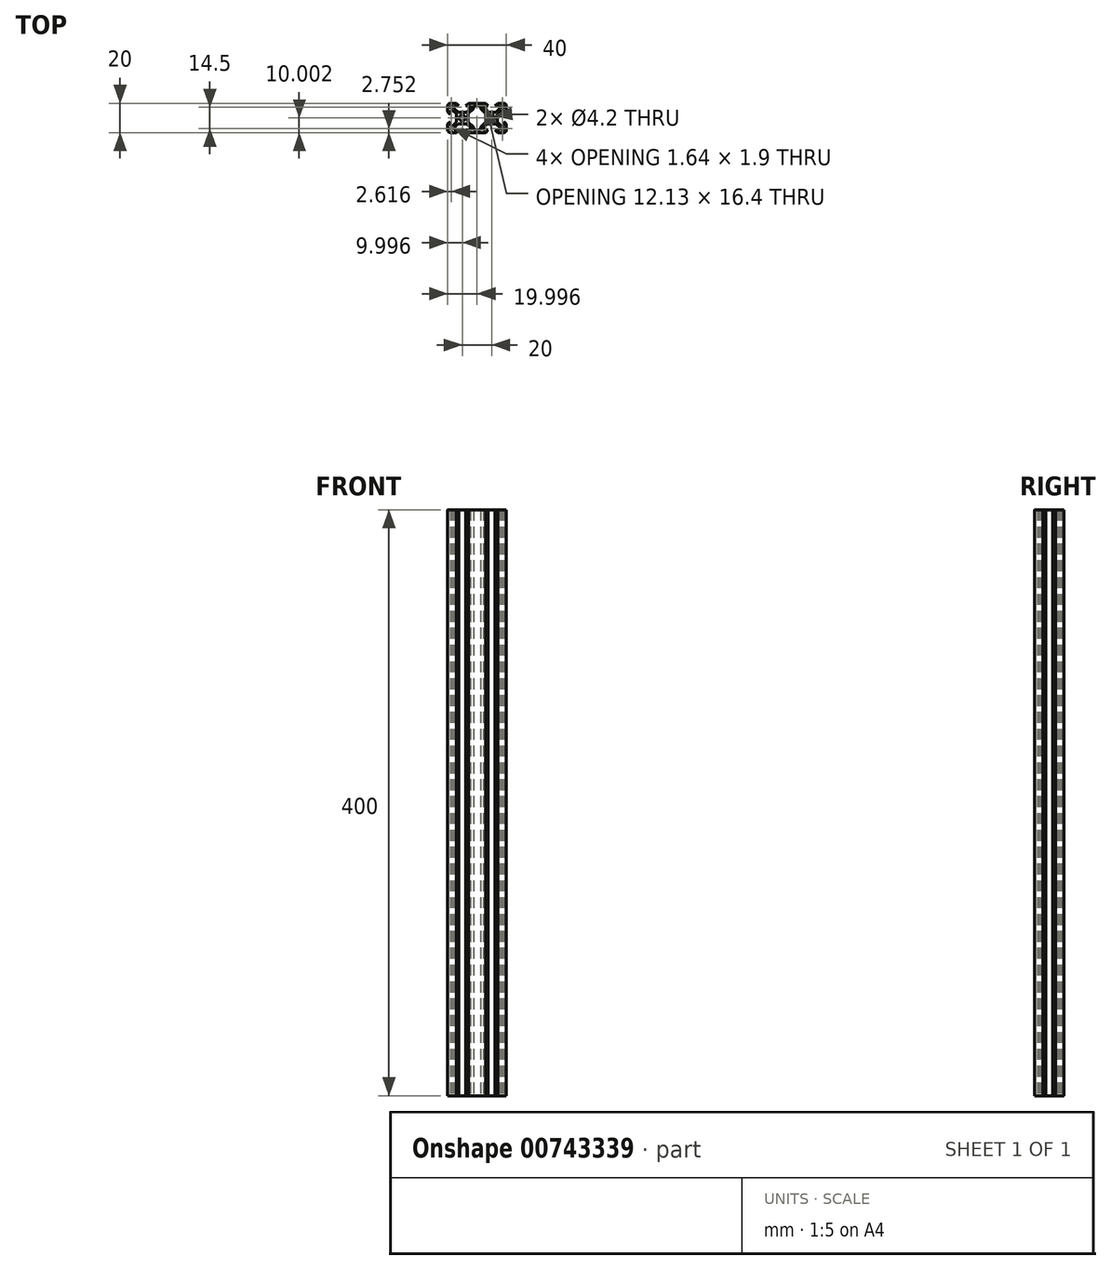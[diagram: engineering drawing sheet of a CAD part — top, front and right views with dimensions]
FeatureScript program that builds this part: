
annotation { "Feature Type Name" : "Feature", "Feature Type Description" : "" }
export const myFeature = defineFeature(function(context is Context, id is Id, definition is map)
    precondition{}
    {
        {
            var Q0;
            Q0=qCreatedBy(makeId("Top.planeOp"),FACE);
            var sketch = newSketch(context, id + "F0", { "sketchPlane" : qUnion([Q0])});
            skLineSegment(sketch, "E0.bottom", {"start": v(-44.81, 11.81) * mm, "end": v(-24.81, 11.81) * mm, "construction": true});
            skLineSegment(sketch, "E0.top", {"start": v(-44.81, -8.19) * mm, "end": v(-24.81, -8.19) * mm, "construction": true});
            skLineSegment(sketch, "E0.left", {"start": v(-44.81, 11.81) * mm, "end": v(-44.81, -8.19) * mm, "construction": true});
            skLineSegment(sketch, "E1", {"start": v(-44.81, 1.81) * mm, "end": v(-30.88, 1.81) * mm, "construction": true});
            skLineSegment(sketch, "E2", {"start": v(-34.81, 11.81) * mm, "end": v(-34.81, -8.19) * mm, "construction": true});
            skArc(sketch, "E3", {"start": v(-34.81, 3.91) * mm, "mid": v(-36.3, 3.3) * mm, "end": v(-36.91, 1.81) * mm});
            skLineSegment(sketch, "E4.left", {"start": v(-44.81, 10.01) * mm, "end": v(-44.81, 6) * mm});
            skLineSegment(sketch, "E4.right", {"start": v(-43.01, 10.01) * mm, "end": v(-43.01, 8.11) * mm});
            skLineSegment(sketch, "E5", {"start": v(-44.81, 11.81) * mm, "end": v(-34.81, 1.81) * mm, "construction": true});
            skLineSegment(sketch, "E6.MirrorCS", {"start": v(-43.01, 10.01) * mm, "end": v(-41.37, 10.01) * mm});
            skLineSegment(sketch, "E7.MirrorCS", {"start": v(-43.01, 11.81) * mm, "end": v(-39, 11.81) * mm});
            skLineSegment(sketch, "E8", {"start": v(-37.2, 10.01) * mm, "end": v(-39, 11.81) * mm});
            skLineSegment(sketch, "E9.MirrorCS", {"start": v(-43.01, 4.2) * mm, "end": v(-44.81, 6) * mm});
            skPoint(sketch, "E10.orphan", {"position": v(-37.2, 11.81) * mm});
            skPoint(sketch, "E11.orphan", {"position": v(-44.81, 4.2) * mm});
            skLineSegment(sketch, "E12.0", {"start": v(-41.3, 7.04) * mm, "end": v(-38.75, 4.65) * mm});
            skLineSegment(sketch, "E13.MirrorCS", {"start": v(-40.3, 8.11) * mm, "end": v(-37.65, 5.74) * mm});
            skPoint(sketch, "E14.orphan", {"position": v(-43.57, 9.18) * mm});
            skPoint(sketch, "E15.orphan", {"position": v(-42.6, 10.16) * mm});
            skLineSegment(sketch, "E16.top", {"start": v(-43.01, 8.11) * mm, "end": v(-42.43, 8.11) * mm});
            skLineSegment(sketch, "E17.MirrorCS", {"start": v(-41.37, 10.01) * mm, "end": v(-41.37, 9.07) * mm});
            skLineSegment(sketch, "E18", {"start": v(-40.3, 8.11) * mm, "end": v(-40.3, 10.01) * mm});
            skLineSegment(sketch, "E19.MirrorCS", {"start": v(-41.3, 7.04) * mm, "end": v(-43.01, 7.04) * mm});
            skLineSegment(sketch, "E20", {"start": v(-42.43, 8.11) * mm, "end": v(-41.37, 9.07) * mm});
            skLineSegment(sketch, "E21.trimOffspring", {"start": v(-43.01, 7.04) * mm, "end": v(-43.01, 4.2) * mm});
            skLineSegment(sketch, "E22.trimOffspring", {"start": v(-40.3, 10.01) * mm, "end": v(-37.2, 10.01) * mm});
            skPoint(sketch, "E16.right.end.orphan", {"position": v(-37.2, 8.37) * mm});
            skPoint(sketch, "E23.MirrorCS.end.orphan", {"position": v(-41.37, 4.2) * mm});
            skPoint(sketch, "E23.MirrorCS.start.orphan", {"position": v(-43.01, 4.2) * mm});
            skLineSegment(sketch, "E24", {"start": v(-38.75, 1.81) * mm, "end": v(-38.75, 4.65) * mm});
            skLineSegment(sketch, "E25.bottom", {"start": v(-37.65, 5.74) * mm, "end": v(-34.81, 5.74) * mm});
            skLineSegment(sketch, "E25.left", {"start": v(-38.75, 4.65) * mm, "end": v(-38.75, 1.81) * mm});
            skPoint(sketch, "E26.orphan", {"position": v(-38.75, 5.74) * mm});
            skPoint(sketch, "E27.orphan", {"position": v(-38.75, -2.12) * mm});
            skPoint(sketch, "E25.right.start.orphan", {"position": v(-30.88, 5.74) * mm});
            skArc(sketch, "E28", {"start": v(-43.01, 11.81) * mm, "mid": v(-44.29, 11.28) * mm, "end": v(-44.81, 10.01) * mm});
            skPoint(sketch, "E29.MirrorCS.start.orphan", {"position": v(-44.81, 11.81) * mm});
            skLineSegment(sketch, "E30.MirrorCS", {"start": v(-26.61, 11.81) * mm, "end": v(-30.62, 11.81) * mm});
            skLineSegment(sketch, "E31.MirrorCS", {"start": v(-32.42, 10.01) * mm, "end": v(-30.62, 11.81) * mm});
            skLineSegment(sketch, "E32.MirrorCS", {"start": v(-29.32, 10.01) * mm, "end": v(-32.42, 10.01) * mm});
            skLineSegment(sketch, "E33.MirrorCS", {"start": v(-29.32, 8.11) * mm, "end": v(-29.32, 10.01) * mm});
            skLineSegment(sketch, "E34.MirrorCS", {"start": v(-29.32, 8.11) * mm, "end": v(-31.98, 5.74) * mm});
            skLineSegment(sketch, "E35.MirrorCS", {"start": v(-31.98, 5.74) * mm, "end": v(-34.81, 5.74) * mm});
            skArc(sketch, "E36.MirrorCS", {"start": v(-34.81, 3.91) * mm, "mid": v(-33.33, 3.3) * mm, "end": v(-32.71, 1.81) * mm});
            skLineSegment(sketch, "E37.MirrorCS", {"start": v(-30.88, 4.65) * mm, "end": v(-30.88, 1.81) * mm});
            skArc(sketch, "E38.MirrorCS", {"start": v(-43.01, -8.19) * mm, "mid": v(-44.29, -7.66) * mm, "end": v(-44.81, -6.39) * mm});
            skLineSegment(sketch, "E39.MirrorCS", {"start": v(-44.81, -6.39) * mm, "end": v(-44.81, -2.38) * mm});
            skLineSegment(sketch, "E40.MirrorCS", {"start": v(-43.01, -0.58) * mm, "end": v(-44.81, -2.38) * mm});
            skLineSegment(sketch, "E41.MirrorCS", {"start": v(-43.01, -3.42) * mm, "end": v(-43.01, -0.58) * mm});
            skLineSegment(sketch, "E42.MirrorCS", {"start": v(-41.3, -3.42) * mm, "end": v(-43.01, -3.42) * mm});
            skLineSegment(sketch, "E43.MirrorCS", {"start": v(-41.3, -3.42) * mm, "end": v(-38.75, -1.03) * mm});
            skLineSegment(sketch, "E44.MirrorCS", {"start": v(-38.75, 1.81) * mm, "end": v(-38.75, -1.03) * mm});
            skLineSegment(sketch, "E45.MirrorCS", {"start": v(-42.43, -4.49) * mm, "end": v(-41.37, -5.44) * mm});
            skLineSegment(sketch, "E46.MirrorCS", {"start": v(-43.01, -4.49) * mm, "end": v(-42.43, -4.49) * mm});
            skLineSegment(sketch, "E47.MirrorCS", {"start": v(-43.01, -6.39) * mm, "end": v(-43.01, -4.49) * mm});
            skLineSegment(sketch, "E48.MirrorCS", {"start": v(-43.01, -6.39) * mm, "end": v(-41.37, -6.39) * mm});
            skLineSegment(sketch, "E49.MirrorCS", {"start": v(-43.01, -8.19) * mm, "end": v(-39, -8.19) * mm});
            skLineSegment(sketch, "E50.MirrorCS", {"start": v(-37.2, -6.39) * mm, "end": v(-39, -8.19) * mm});
            skLineSegment(sketch, "E51.MirrorCS", {"start": v(-40.3, -6.39) * mm, "end": v(-37.2, -6.39) * mm});
            skLineSegment(sketch, "E52.MirrorCS", {"start": v(-40.3, -4.49) * mm, "end": v(-40.3, -6.39) * mm});
            skLineSegment(sketch, "E53.MirrorCS", {"start": v(-40.3, -4.49) * mm, "end": v(-37.65, -2.12) * mm});
            skLineSegment(sketch, "E54.MirrorCS", {"start": v(-37.65, -2.12) * mm, "end": v(-34.81, -2.12) * mm});
            skArc(sketch, "E55.MirrorCS", {"start": v(-34.81, -0.29) * mm, "mid": v(-36.3, 0.33) * mm, "end": v(-36.91, 1.81) * mm});
            skLineSegment(sketch, "E56.MirrorCS", {"start": v(-41.37, -6.39) * mm, "end": v(-41.37, -5.44) * mm});
            skLineSegment(sketch, "E57.MirrorCS", {"start": v(-8.25, -6.39) * mm, "end": v(-8.25, -5.44) * mm});
            skLineSegment(sketch, "E58.MirrorCS", {"start": v(-8.25, 10.01) * mm, "end": v(-8.25, 9.07) * mm});
            skLineSegment(sketch, "E59.MirrorCS", {"start": v(-6.61, 8.11) * mm, "end": v(-7.2, 8.11) * mm});
            skLineSegment(sketch, "E60.MirrorCS", {"start": v(-6.61, -4.49) * mm, "end": v(-7.2, -4.49) * mm});
            skLineSegment(sketch, "E61.MirrorCS", {"start": v(-6.61, -8.19) * mm, "end": v(-10.62, -8.19) * mm});
            skLineSegment(sketch, "E62.MirrorCS", {"start": v(-23.01, 11.81) * mm, "end": v(-19, 11.81) * mm});
            skLineSegment(sketch, "E63.MirrorCS", {"start": v(-4.81, 10.01) * mm, "end": v(-4.81, 6) * mm});
            skLineSegment(sketch, "E64.MirrorCS", {"start": v(-6.61, 11.81) * mm, "end": v(-10.62, 11.81) * mm});
            skLineSegment(sketch, "E65.MirrorCS", {"start": v(-4.81, -6.39) * mm, "end": v(-4.81, -2.38) * mm});
            skLineSegment(sketch, "E66.MirrorCS", {"start": v(-6.61, 10.01) * mm, "end": v(-6.61, 8.11) * mm});
            skLineSegment(sketch, "E67.MirrorCS", {"start": v(-10.88, 1.81) * mm, "end": v(-10.88, 4.65) * mm});
            skPoint(sketch, "E68.MirrorP", {"position": v(-8.25, 4.2) * mm});
            skLineSegment(sketch, "E69.MirrorCS", {"start": v(-9.32, 10.01) * mm, "end": v(-12.42, 10.01) * mm});
            skLineSegment(sketch, "E70.MirrorCS", {"start": v(-6.61, 10.01) * mm, "end": v(-8.25, 10.01) * mm});
            skPoint(sketch, "E71.MirrorP", {"position": v(-6.05, 9.18) * mm});
            skLineSegment(sketch, "E72.MirrorCS", {"start": v(-9.32, -6.39) * mm, "end": v(-12.42, -6.39) * mm});
            skLineSegment(sketch, "E73.MirrorCS", {"start": v(-8.33, 7.04) * mm, "end": v(-10.88, 4.65) * mm});
            skLineSegment(sketch, "E74.MirrorCS", {"start": v(-8.33, 7.04) * mm, "end": v(-6.61, 7.04) * mm});
            skLineSegment(sketch, "E75.MirrorCS", {"start": v(-20.3, 10.01) * mm, "end": v(-17.2, 10.01) * mm});
            skLineSegment(sketch, "E76.MirrorCS", {"start": v(-8.33, -3.42) * mm, "end": v(-6.61, -3.42) * mm});
            skArc(sketch, "E77.MirrorCS", {"start": v(-6.61, 11.81) * mm, "mid": v(-5.34, 11.28) * mm, "end": v(-4.81, 10.01) * mm});
            skLineSegment(sketch, "E78.MirrorCS", {"start": v(-12.42, -6.39) * mm, "end": v(-10.62, -8.19) * mm});
            skLineSegment(sketch, "E79.MirrorCS", {"start": v(-6.61, 4.2) * mm, "end": v(-4.81, 6) * mm});
            skPoint(sketch, "E80.MirrorP", {"position": v(-10.88, -2.12) * mm});
            skLineSegment(sketch, "E81.MirrorCS", {"start": v(-9.32, 8.11) * mm, "end": v(-9.32, 10.01) * mm});
            skLineSegment(sketch, "E82.MirrorCS", {"start": v(-17.2, 10.01) * mm, "end": v(-19, 11.81) * mm});
            skLineSegment(sketch, "E83.MirrorCS", {"start": v(-6.61, -3.42) * mm, "end": v(-6.61, -0.58) * mm});
            skPoint(sketch, "E84.MirrorP", {"position": v(-4.81, 4.2) * mm});
            skLineSegment(sketch, "E85.MirrorCS", {"start": v(-10.88, 4.65) * mm, "end": v(-10.88, 1.81) * mm});
            skLineSegment(sketch, "E86.MirrorCS", {"start": v(-12.42, 10.01) * mm, "end": v(-10.62, 11.81) * mm});
            skPoint(sketch, "E87.MirrorP", {"position": v(-10.88, 5.74) * mm});
            skLineSegment(sketch, "E88.MirrorCS", {"start": v(-6.61, -0.58) * mm, "end": v(-4.81, -2.38) * mm});
            skPoint(sketch, "E89.MirrorP", {"position": v(-12.42, 11.81) * mm});
            skArc(sketch, "E90.MirrorCS", {"start": v(-14.81, 3.91) * mm, "mid": v(-13.33, 3.3) * mm, "end": v(-12.71, 1.81) * mm});
            skLineSegment(sketch, "E91.MirrorCS", {"start": v(-14.81, 11.81) * mm, "end": v(-14.81, -8.19) * mm, "construction": true});
            skLineSegment(sketch, "E92.MirrorCS", {"start": v(-4.81, 1.81) * mm, "end": v(-18.75, 1.81) * mm, "construction": true});
            skLineSegment(sketch, "E93.MirrorCS", {"start": v(-4.81, 11.81) * mm, "end": v(-4.81, -8.19) * mm, "construction": true});
            skLineSegment(sketch, "E94.MirrorCS", {"start": v(-4.81, -8.19) * mm, "end": v(-24.81, -8.19) * mm, "construction": true});
            skLineSegment(sketch, "E95.MirrorCS", {"start": v(-4.81, 11.81) * mm, "end": v(-24.81, 11.81) * mm, "construction": true});
            skLineSegment(sketch, "E96.MirrorCS", {"start": v(-4.81, 11.81) * mm, "end": v(-14.81, 1.81) * mm, "construction": true});
            skLineSegment(sketch, "E97.MirrorCS", {"start": v(-11.98, 5.74) * mm, "end": v(-14.81, 5.74) * mm});
            skArc(sketch, "E98.MirrorCS", {"start": v(-14.81, -0.29) * mm, "mid": v(-13.33, 0.33) * mm, "end": v(-12.71, 1.81) * mm});
            skLineSegment(sketch, "E99.MirrorCS", {"start": v(-6.61, -6.39) * mm, "end": v(-8.25, -6.39) * mm});
            skLineSegment(sketch, "E100.MirrorCS", {"start": v(-18.75, 4.65) * mm, "end": v(-18.75, 1.81) * mm});
            skArc(sketch, "E101.MirrorCS", {"start": v(-6.61, -8.19) * mm, "mid": v(-5.34, -7.66) * mm, "end": v(-4.81, -6.39) * mm});
            skLineSegment(sketch, "E102.MirrorCS", {"start": v(-11.98, -2.12) * mm, "end": v(-14.81, -2.12) * mm});
            skLineSegment(sketch, "E103.MirrorCS", {"start": v(-6.61, -6.39) * mm, "end": v(-6.61, -4.49) * mm});
            skLineSegment(sketch, "E104.MirrorCS", {"start": v(-17.65, 5.74) * mm, "end": v(-14.81, 5.74) * mm});
            skLineSegment(sketch, "E105.MirrorCS", {"start": v(-7.2, -4.49) * mm, "end": v(-8.25, -5.44) * mm});
            skPoint(sketch, "E106.MirrorP", {"position": v(-4.81, 11.81) * mm});
            skPoint(sketch, "E107.MirrorP", {"position": v(-12.42, 8.37) * mm});
            skArc(sketch, "E108.MirrorCS", {"start": v(-14.81, 3.91) * mm, "mid": v(-16.3, 3.3) * mm, "end": v(-16.91, 1.81) * mm});
            skLineSegment(sketch, "E109.MirrorCS", {"start": v(-9.32, -4.49) * mm, "end": v(-11.98, -2.12) * mm});
            skLineSegment(sketch, "E110.MirrorCS", {"start": v(-6.61, 7.04) * mm, "end": v(-6.61, 4.2) * mm});
            skLineSegment(sketch, "E111.MirrorCS", {"start": v(-20.3, 8.11) * mm, "end": v(-17.65, 5.74) * mm});
            skLineSegment(sketch, "E112.MirrorCS", {"start": v(-10.88, 1.81) * mm, "end": v(-10.88, -1.03) * mm});
            skPoint(sketch, "E113.MirrorP", {"position": v(-6.61, 4.2) * mm});
            skPoint(sketch, "E114.MirrorP", {"position": v(-7.03, 10.16) * mm});
            skLineSegment(sketch, "E115.MirrorCS", {"start": v(-9.32, -4.49) * mm, "end": v(-9.32, -6.39) * mm});
            skLineSegment(sketch, "E116.MirrorCS", {"start": v(-9.32, 8.11) * mm, "end": v(-11.98, 5.74) * mm});
            skLineSegment(sketch, "E117.MirrorCS", {"start": v(-7.2, 8.11) * mm, "end": v(-8.25, 9.07) * mm});
            skLineSegment(sketch, "E118.MirrorCS", {"start": v(-20.3, 8.11) * mm, "end": v(-20.3, 10.01) * mm});
            skLineSegment(sketch, "E119.MirrorCS", {"start": v(-8.33, -3.42) * mm, "end": v(-10.88, -1.03) * mm});
            skPoint(sketch, "E120.MirrorP", {"position": v(-18.75, 5.74) * mm});
            skLineSegment(sketch, "E121", {"start": v(-26.61, 11.81) * mm, "end": v(-23.01, 11.81) * mm});
            skLineSegment(sketch, "E122", {"start": v(-27.2, 8.11) * mm, "end": v(-27.2, 10.01) * mm});
            skPoint(sketch, "E123.MirrorCS.end.orphan", {"position": v(-28.25, 9.07) * mm});
            skPoint(sketch, "E124.orphan", {"position": v(-28.25, 10.01) * mm});
            skPoint(sketch, "E125.MirrorCS.start.orphan", {"position": v(-26.61, 8.11) * mm});
            skPoint(sketch, "E126.MirrorCS.end.orphan", {"position": v(-26.61, 4.2) * mm});
            skPoint(sketch, "E126.MirrorCS.start.orphan", {"position": v(-26.61, 7.04) * mm});
            skPoint(sketch, "E127.MirrorCS.start.orphan", {"position": v(-23.01, 4.2) * mm});
            skLineSegment(sketch, "E128", {"start": v(-22.43, 8.11) * mm, "end": v(-22.43, 10.01) * mm});
            skPoint(sketch, "E129.MirrorCS.start.orphan", {"position": v(-23.01, 7.04) * mm});
            skPoint(sketch, "E130.MirrorCS.start.orphan", {"position": v(-21.37, 10.01) * mm});
            skPoint(sketch, "E131.MirrorCS.end.orphan", {"position": v(-21.37, 9.07) * mm});
            skPoint(sketch, "E132.MirrorCS.start.orphan", {"position": v(-23.01, 8.11) * mm});
            skPoint(sketch, "E133.MirrorP", {"position": v(-23.01, -0.58) * mm});
            skPoint(sketch, "E134.MirrorP", {"position": v(-26.61, -0.58) * mm});
            skLineSegment(sketch, "E135.MirrorCS", {"start": v(-20.3, -4.49) * mm, "end": v(-17.65, -2.12) * mm});
            skPoint(sketch, "E136.MirrorP", {"position": v(-30.88, -2.12) * mm});
            skLineSegment(sketch, "E137.MirrorCS", {"start": v(-29.32, -4.49) * mm, "end": v(-29.32, -6.39) * mm});
            skPoint(sketch, "E138.MirrorP", {"position": v(-26.61, -3.42) * mm});
            skLineSegment(sketch, "E139.MirrorCS", {"start": v(-29.32, -4.49) * mm, "end": v(-31.98, -2.12) * mm});
            skLineSegment(sketch, "E140.MirrorCS", {"start": v(-23.01, -8.19) * mm, "end": v(-19, -8.19) * mm});
            skLineSegment(sketch, "E141.MirrorCS", {"start": v(-17.2, -6.39) * mm, "end": v(-19, -8.19) * mm});
            skLineSegment(sketch, "E142.MirrorCS", {"start": v(-26.61, -8.19) * mm, "end": v(-30.62, -8.19) * mm});
            skLineSegment(sketch, "E143.MirrorCS", {"start": v(-27.2, -4.49) * mm, "end": v(-27.2, -6.39) * mm});
            skPoint(sketch, "E144.MirrorP", {"position": v(-26.61, -4.49) * mm});
            skPoint(sketch, "E145.MirrorP", {"position": v(-21.37, -6.39) * mm});
            skPoint(sketch, "E146.MirrorP", {"position": v(-28.25, -5.44) * mm});
            skLineSegment(sketch, "E147.MirrorCS", {"start": v(-26.61, -8.19) * mm, "end": v(-23.01, -8.19) * mm});
            skPoint(sketch, "E148.MirrorP", {"position": v(-18.75, -2.12) * mm});
            skLineSegment(sketch, "E149.MirrorCS", {"start": v(-29.32, -6.39) * mm, "end": v(-32.42, -6.39) * mm});
            skPoint(sketch, "E150.MirrorP", {"position": v(-23.01, -3.42) * mm});
            skLineSegment(sketch, "E151.MirrorCS", {"start": v(-32.42, -6.39) * mm, "end": v(-30.62, -8.19) * mm});
            skLineSegment(sketch, "E152.MirrorCS", {"start": v(-20.3, -4.49) * mm, "end": v(-20.3, -6.39) * mm});
            skPoint(sketch, "E153.MirrorP", {"position": v(-28.25, -6.39) * mm});
            skLineSegment(sketch, "E154.MirrorCS", {"start": v(-22.43, -4.49) * mm, "end": v(-22.43, -6.39) * mm});
            skLineSegment(sketch, "E155.MirrorCS", {"start": v(-20.3, -6.39) * mm, "end": v(-17.2, -6.39) * mm});
            skPoint(sketch, "E156.MirrorP", {"position": v(-21.37, -5.44) * mm});
            skPoint(sketch, "E157.MirrorP", {"position": v(-23.01, -4.49) * mm});
            skLineSegment(sketch, "E158.MirrorCS", {"start": v(-31.98, -2.12) * mm, "end": v(-34.81, -2.12) * mm});
            skArc(sketch, "E159.MirrorCS", {"start": v(-34.81, -0.29) * mm, "mid": v(-33.33, 0.33) * mm, "end": v(-32.71, 1.81) * mm});
            skLineSegment(sketch, "E160.MirrorCS", {"start": v(-30.88, -1.03) * mm, "end": v(-30.88, 1.81) * mm});
            skLineSegment(sketch, "E161.MirrorCS", {"start": v(-18.75, -1.03) * mm, "end": v(-18.75, 1.81) * mm});
            skArc(sketch, "E162.MirrorCS", {"start": v(-14.81, -0.29) * mm, "mid": v(-16.3, 0.33) * mm, "end": v(-16.91, 1.81) * mm});
            skLineSegment(sketch, "E163.MirrorCS", {"start": v(-17.65, -2.12) * mm, "end": v(-14.81, -2.12) * mm});
            skPoint(sketch, "E164.orphan", {"position": v(-23.01, -6.39) * mm});
            skPoint(sketch, "E165.MirrorCS.start.orphan", {"position": v(-26.61, -6.39) * mm});
            skPoint(sketch, "E166.orphan", {"position": v(-23.01, 10.01) * mm});
            skPoint(sketch, "E167.start.orphan", {"position": v(-26.61, 10.01) * mm});
            skLineSegment(sketch, "E168", {"start": v(-27.2, 10.01) * mm, "end": v(-22.43, 10.01) * mm});
            skLineSegment(sketch, "E169", {"start": v(-27.2, -6.39) * mm, "end": v(-22.43, -6.39) * mm});
            skPoint(sketch, "E170.MirrorCS.start.orphan", {"position": v(-28.33, 7.04) * mm});
            skPoint(sketch, "E171.MirrorCS.start.orphan", {"position": v(-21.3, 7.04) * mm});
            skPoint(sketch, "E172.MirrorCS.end.orphan", {"position": v(-30.88, -1.03) * mm});
            skPoint(sketch, "E172.MirrorCS.start.orphan", {"position": v(-28.33, -3.42) * mm});
            skPoint(sketch, "E173.MirrorCS.end.orphan", {"position": v(-18.75, -1.03) * mm});
            skPoint(sketch, "E173.MirrorCS.start.orphan", {"position": v(-21.3, -3.42) * mm});
            skLineSegment(sketch, "E174", {"start": v(-30.88, 4.65) * mm, "end": v(-27.2, 8.11) * mm});
            skLineSegment(sketch, "E175", {"start": v(-22.43, 8.11) * mm, "end": v(-18.75, 4.65) * mm});
            skLineSegment(sketch, "E176", {"start": v(-18.75, -1.03) * mm, "end": v(-22.43, -4.49) * mm});
            skLineSegment(sketch, "E177", {"start": v(-27.2, -4.49) * mm, "end": v(-30.88, -1.03) * mm});
            skPoint(sketch, "E178.MirrorCS.end.orphan", {"position": v(-24.81, 6) * mm});
            skPoint(sketch, "E178.MirrorCS.start.orphan", {"position": v(-24.81, 10.01) * mm});
            skPoint(sketch, "E179.orphan", {"position": v(-24.81, 1.81) * mm});
            skSolve(sketch);
        }
        {
            var Q0;
            Q0=qSketchRegion(id+"F0",true);
            extrude(context, id + "F1", {"entities" : qUnion([Q0]), "depth" : 400 * mm, "offsetDistance" : 25 * mm});
        }
    });
